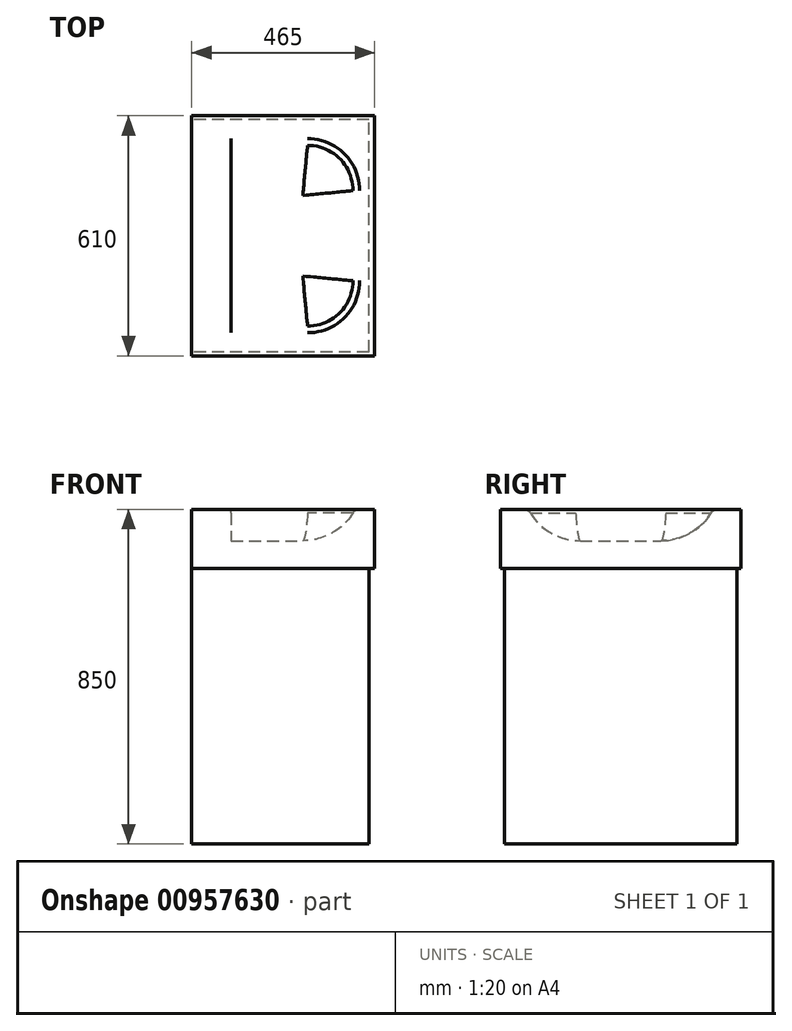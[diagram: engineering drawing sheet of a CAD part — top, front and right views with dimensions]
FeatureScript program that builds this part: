
annotation { "Feature Type Name" : "Feature", "Feature Type Description" : "" }
export const myFeature = defineFeature(function(context is Context, id is Id, definition is map)
    precondition{}
    {
        {
            var Q0;
            Q0=qCreatedBy(makeId("Right.planeOp"),FACE);
            var sketch = newSketch(context, id + "F0", { "sketchPlane" : qUnion([Q0])});
            skLineSegment(sketch, "E0.bottom", {"start": v(-305, 700) * mm, "end": v(-295, 700) * mm});
            skLineSegment(sketch, "E0.top", {"start": v(-305, 850) * mm, "end": v(305, 850) * mm});
            skLineSegment(sketch, "E0.left", {"start": v(-305, 700) * mm, "end": v(-305, 850) * mm});
            skLineSegment(sketch, "E0.right", {"start": v(305, 700) * mm, "end": v(305, 850) * mm});
            skPoint(sketch, "E0.middle", {"position": v(0, 775) * mm});
            skLineSegment(sketch, "E1.top", {"start": v(-295, 0) * mm, "end": v(295, 0) * mm});
            skLineSegment(sketch, "E1.left", {"start": v(-295, 700) * mm, "end": v(-295, 0) * mm});
            skLineSegment(sketch, "E1.right", {"start": v(295, 700) * mm, "end": v(295, 0) * mm});
            skPoint(sketch, "E1.middle", {"position": v(0, 350) * mm});
            skLineSegment(sketch, "E2.trimOffspring", {"start": v(295, 700) * mm, "end": v(305, 700) * mm});
            skSolve(sketch);
        }
        {
            var Q0;
            Q0=makeQuery(id+"F0.imprint","IMPRINT",FACE,{"disambiguationData":[TD([[makeQuery(id+"F0.imprint","IMPRINT",EDGE,{"derivedFrom":sQuery(id+"F0.wireOp",EDGE,"E0.bottom")}),1.0]])]});
            extrude(context, id + "F1", {"entities" : qUnion([Q0]), "depth" : 225 * mm, "offsetDistance" : 25 * mm, "hasSecondDirection" : true, "secondDirectionOppositeDirection" : true, "secondDirectionDepth" : 225 * mm});
        }
        {
            var Q0;
            Q0=makeQuery(id+"F1.opExtrude","CAP_FACE",FACE,{"disambiguationData":[OSD([sQuery(id+"F0.wireOp",EDGE,"E0.bottom"),sQuery(id+"F0.wireOp",EDGE,"E0.top"),sQuery(id+"F0.wireOp",EDGE,"E0.left"),sQuery(id+"F0.wireOp",EDGE,"E0.right"),sQuery(id+"F0.wireOp",EDGE,"E1.top"),sQuery(id+"F0.wireOp",EDGE,"E1.left"),sQuery(id+"F0.wireOp",EDGE,"E1.right"),sQuery(id+"F0.wireOp",EDGE,"E2.trimOffspring")])],"isStart":false});
            var sketch = newSketch(context, id + "F2", { "sketchPlane" : qUnion([Q0])});
            skLineSegment(sketch, "E3.bottom", {"start": v(-305, 850) * mm, "end": v(305, 850) * mm});
            skLineSegment(sketch, "E3.top", {"start": v(-305, 700) * mm, "end": v(305, 700) * mm});
            skLineSegment(sketch, "E3.left", {"start": v(-305, 850) * mm, "end": v(-305, 700) * mm});
            skLineSegment(sketch, "E3.right", {"start": v(305, 850) * mm, "end": v(305, 700) * mm});
            skSolve(sketch);
        }
        {
            var Q0;
            Q0=makeQuery(id+"F2.imprint","IMPRINT",FACE,{"disambiguationData":[TD([[makeQuery(id+"F2.imprint","IMPRINT",EDGE,{"derivedFrom":sQuery(id+"F2.wireOp",EDGE,"E3.bottom")}),-1.0]])]});
            extrude(context, id + "F3", {"entities" : qUnion([Q0]), "operationType" : NewBodyOperationType.ADD, "depth" : 15 * mm, "offsetDistance" : 25 * mm});
        }
        {
            var Q0;
            Q0=makeQuery(id+"F3.boolean.opBoolean","MERGE",FACE,{"derivedFrom":[makeQuery(id+"F1.opExtrude","SWEPT_FACE",FACE,{"disambiguationData":[OSD([sQuery(id+"F0.wireOp",EDGE,"E0.top")])]}),makeQuery(id+"F3.opExtrude","SWEPT_FACE",FACE,{"disambiguationData":[OSD([sQuery(id+"F2.wireOp",EDGE,"E3.bottom")])]})]});
            var sketch = newSketch(context, id + "F4", { "sketchPlane" : qUnion([Q0])});
            skLineSegment(sketch, "E4.bottom", {"start": v(-125, -235) * mm, "end": v(190, -235) * mm});
            skLineSegment(sketch, "E4.top", {"start": v(-125, 235) * mm, "end": v(190, 235) * mm});
            skLineSegment(sketch, "E4.left", {"start": v(-125, -235) * mm, "end": v(-125, 235) * mm});
            skLineSegment(sketch, "E4.right", {"start": v(190, -235) * mm, "end": v(190, 235) * mm});
            skPoint(sketch, "E4.middle", {"position": v(32.5, 0) * mm});
            skSolve(sketch);
        }
        {
            var Q0;
            Q0=makeQuery(id+"F4.imprint","IMPRINT",FACE,{"disambiguationData":[TD([[makeQuery(id+"F4.imprint","IMPRINT",EDGE,{"derivedFrom":sQuery(id+"F4.wireOp",EDGE,"E4.bottom")}),1.0]])]});
            extrude(context, id + "F5", {"entities" : qUnion([Q0]), "operationType" : NewBodyOperationType.REMOVE, "oppositeDirection" : true, "depth" : 80 * mm, "offsetDistance" : 25 * mm});
        }
        {
            var Q0;
            Q0=makeQuery(id+"F5.boolean.opBoolean","COPY",EDGE,{"derivedFrom":makeQuery(id+"F5.opExtrude","SWEPT_EDGE",EDGE,{"disambiguationData":[OSD([sQuery(id+"F4.wireOp",EDGE,"E4.bottom"),sQuery(id+"F4.wireOp",EDGE,"E4.right")])]})});
            var Q1;
            Q1=makeQuery(id+"F5.boolean.opBoolean","COPY",EDGE,{"derivedFrom":makeQuery(id+"F5.opExtrude","SWEPT_EDGE",EDGE,{"disambiguationData":[OSD([sQuery(id+"F4.wireOp",EDGE,"E4.top"),sQuery(id+"F4.wireOp",EDGE,"E4.right")])]})});
            fillet(context, id + "F6", {"entities" : qUnion([Q0, Q1]), "radius" : 120 * mm, "tangentPropagation" : true, "allowEdgeOverflow" : false});
        }
        {
            var Q0;
            {var subQ0=sQuery(id+"F4.wireOp",EDGE,"E4.right");var subQ1=sQuery(id+"F4.wireOp",EDGE,"E4.top");Q0=makeQuery(id+"F6.opFillet","BLEND_EDGE",EDGE,{"blendedFrom":[makeQuery(id+"F5.boolean.opBoolean","COPY",EDGE,{"derivedFrom":makeQuery(id+"F5.opExtrude","SWEPT_EDGE",EDGE,{"disambiguationData":[OSD([subQ1,subQ0])]})}),makeQuery(id+"F5.boolean.opBoolean","COPY",FACE,{"derivedFrom":makeQuery(id+"F5.opExtrude","CAP_FACE",FACE,{"disambiguationData":[OSD([sQuery(id+"F4.wireOp",EDGE,"E4.bottom"),subQ1,sQuery(id+"F4.wireOp",EDGE,"E4.left"),subQ0])],"isStart":false})})],"blendedInto":[makeQuery(id+"F5.boolean.opBoolean","COPY",FACE,{"derivedFrom":makeQuery(id+"F5.opExtrude","CAP_FACE",FACE,{"disambiguationData":[OSD([sQuery(id+"F4.wireOp",EDGE,"E4.bottom"),subQ1,sQuery(id+"F4.wireOp",EDGE,"E4.left"),subQ0])],"isStart":false})})]});}
            fillet(context, id + "F7", {"entities" : qUnion([Q0]), "radius" : 150 * mm, "tangentPropagation" : true, "allowEdgeOverflow" : false});
        }
        {
            var Q0;
            Q0=makeQuery(id+"F5.boolean.opBoolean","COPY",EDGE,{"derivedFrom":makeQuery(id+"F5.opExtrude","CAP_EDGE",EDGE,{"disambiguationData":[OSD([sQuery(id+"F4.wireOp",EDGE,"E4.left")])],"isStart":true})});
            var Q1;
            Q1=makeQuery(id+"F7.opFillet","BLEND_EDGE",EDGE,{"blendedFrom":[makeQuery(id+"F5.boolean.opBoolean","COPY",EDGE,{"derivedFrom":makeQuery(id+"F5.opExtrude","CAP_EDGE",EDGE,{"disambiguationData":[OSD([sQuery(id+"F4.wireOp",EDGE,"E4.bottom")])],"isStart":false})}),makeQuery(id+"F3.boolean.opBoolean","MERGE",FACE,{"derivedFrom":[makeQuery(id+"F1.opExtrude","SWEPT_FACE",FACE,{"disambiguationData":[OSD([sQuery(id+"F0.wireOp",EDGE,"E0.top")])]}),makeQuery(id+"F3.opExtrude","SWEPT_FACE",FACE,{"disambiguationData":[OSD([sQuery(id+"F2.wireOp",EDGE,"E3.bottom")])]})]})],"blendedInto":[makeQuery(id+"F3.boolean.opBoolean","MERGE",FACE,{"derivedFrom":[makeQuery(id+"F1.opExtrude","SWEPT_FACE",FACE,{"disambiguationData":[OSD([sQuery(id+"F0.wireOp",EDGE,"E0.top")])]}),makeQuery(id+"F3.opExtrude","SWEPT_FACE",FACE,{"disambiguationData":[OSD([sQuery(id+"F2.wireOp",EDGE,"E3.bottom")])]})]})]});
            fillet(context, id + "F8", {"entities" : qUnion([Q0, Q1]), "radius" : 20 * mm, "tangentPropagation" : true, "allowEdgeOverflow" : false});
        }
    });
